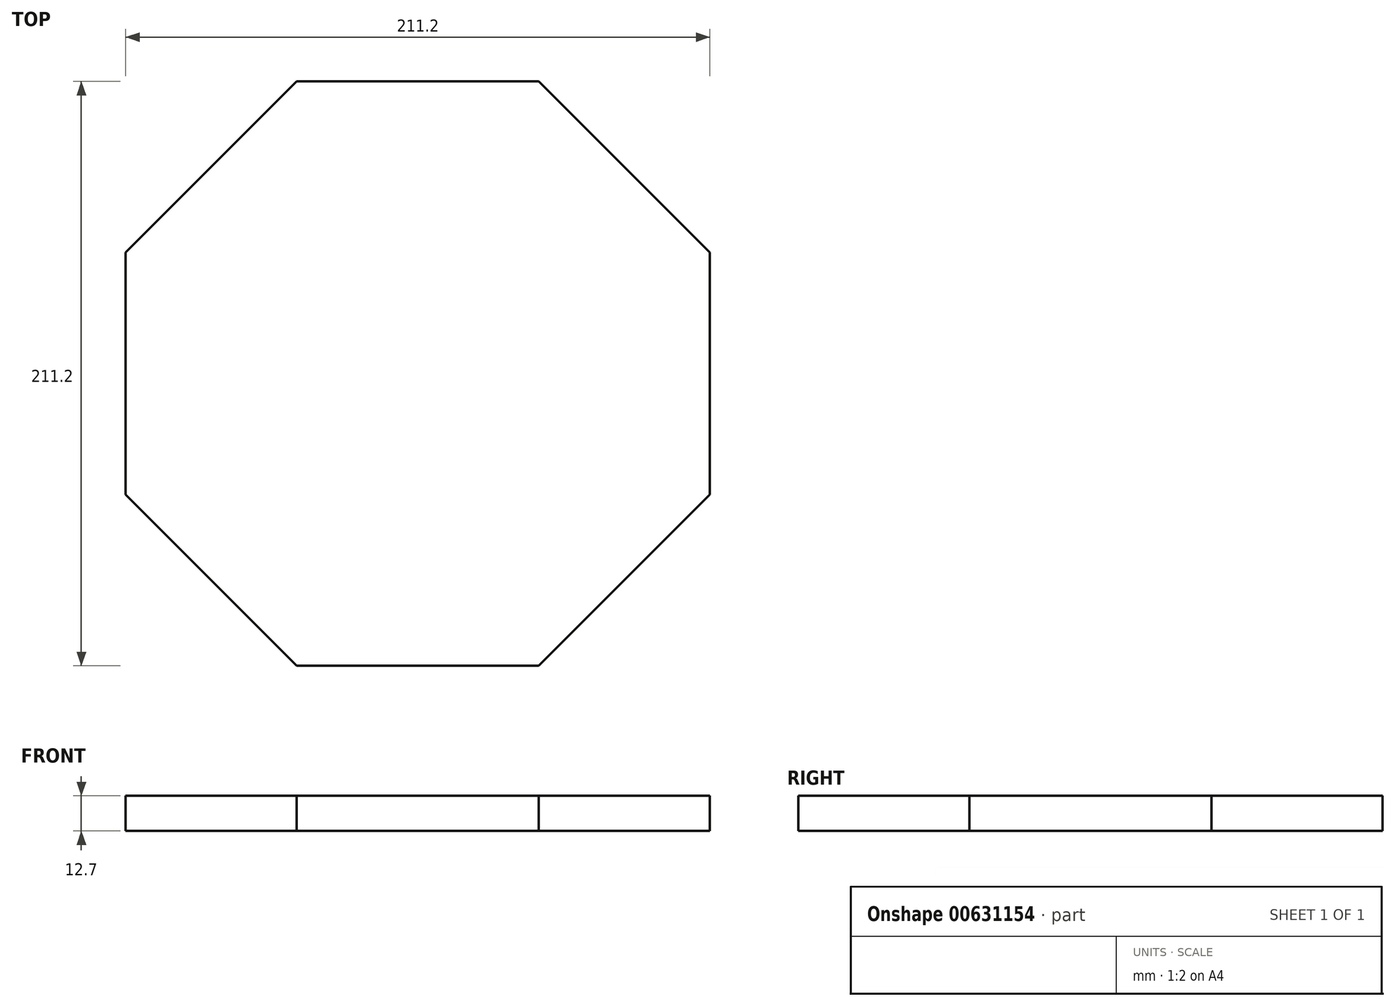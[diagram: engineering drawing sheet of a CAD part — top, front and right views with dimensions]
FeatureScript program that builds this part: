
annotation { "Feature Type Name" : "Feature", "Feature Type Description" : "" }
export const myFeature = defineFeature(function(context is Context, id is Id, definition is map)
    precondition{}
    {
        {
            var Q0;
            Q0=qCreatedBy(makeId("Top.planeOp"),FACE);
            var sketch = newSketch(context, id + "F0", { "sketchPlane" : qUnion([Q0])});
            skLineSegment(sketch, "E0", {"start": v(-52.54, 114.4) * mm, "end": v(34.94, 114.4) * mm});
            skLineSegment(sketch, "E1", {"start": v(34.94, 114.4) * mm, "end": v(96.8, 52.54) * mm});
            skLineSegment(sketch, "E2", {"start": v(96.8, 52.54) * mm, "end": v(96.8, -34.94) * mm});
            skLineSegment(sketch, "E3", {"start": v(96.8, -34.94) * mm, "end": v(34.94, -96.8) * mm});
            skLineSegment(sketch, "E4", {"start": v(34.94, -96.8) * mm, "end": v(-52.54, -96.8) * mm});
            skLineSegment(sketch, "E5", {"start": v(-52.54, -96.8) * mm, "end": v(-114.4, -34.94) * mm});
            skLineSegment(sketch, "E6", {"start": v(-114.4, -34.94) * mm, "end": v(-114.4, 52.54) * mm});
            skLineSegment(sketch, "E7", {"start": v(-114.4, 52.54) * mm, "end": v(-52.54, 114.4) * mm});
            skSolve(sketch);
        }
        {
            var Q0;
            Q0=makeQuery(id+"F0.imprint","IMPRINT",FACE,{"disambiguationData":[TD([[makeQuery(id+"F0.imprint","IMPRINT",EDGE,{"derivedFrom":sQuery(id+"F0.wireOp",EDGE,"E0")}),-1.0]])]});
            extrude(context, id + "F1", {"entities" : qUnion([Q0]), "depth" : 12.7 * mm, "offsetDistance" : 25.4 * mm});
        }
    });
